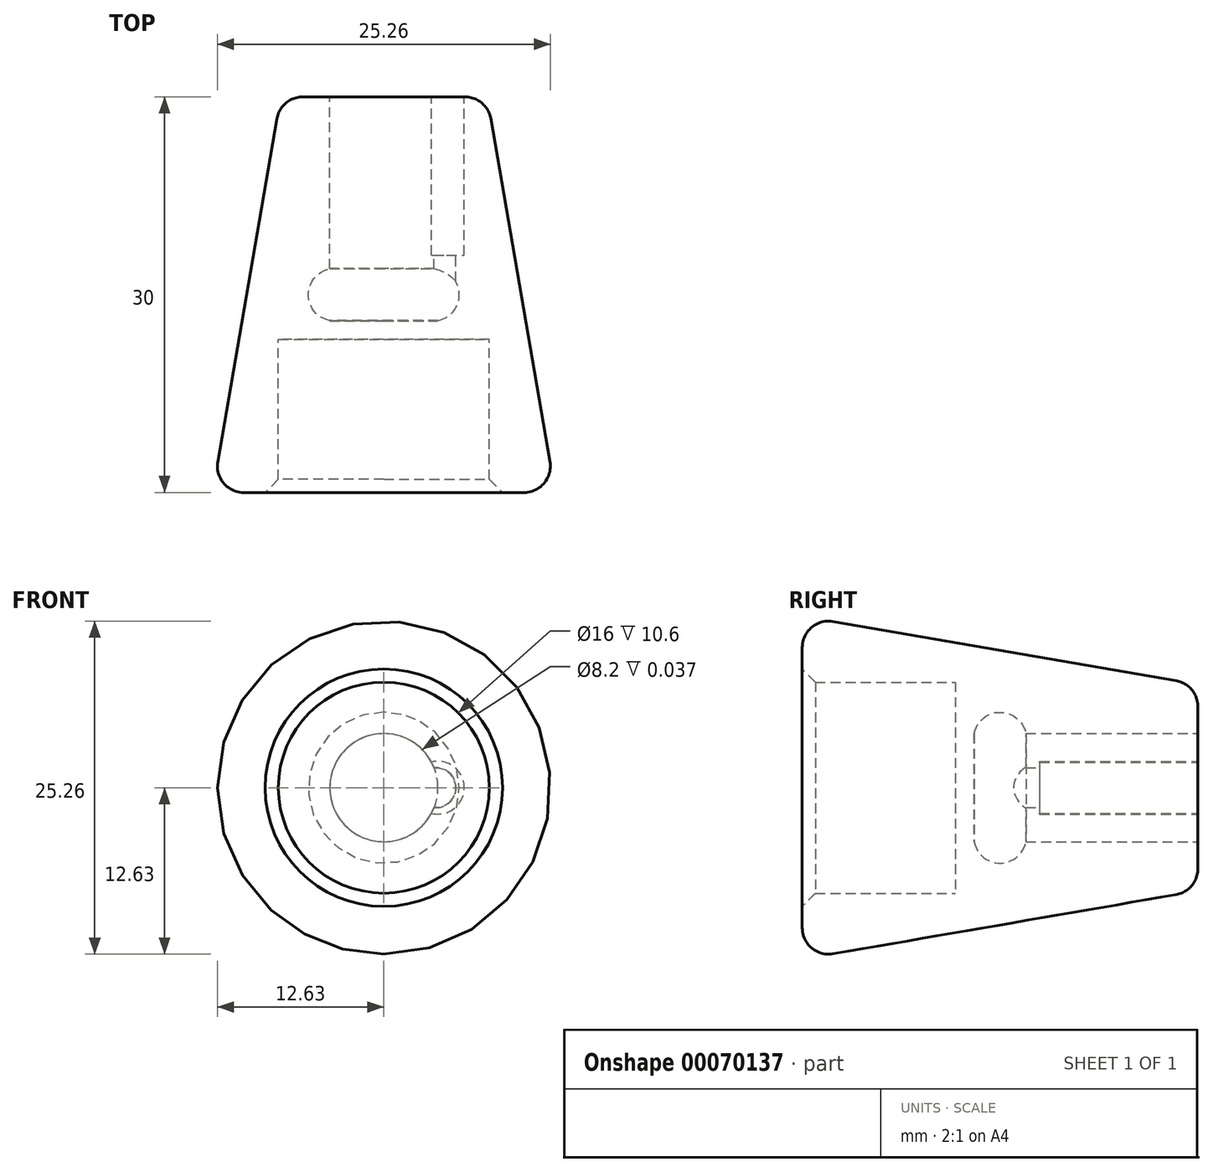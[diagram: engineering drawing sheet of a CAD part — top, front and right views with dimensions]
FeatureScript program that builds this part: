
annotation { "Feature Type Name" : "Feature", "Feature Type Description" : "" }
export const myFeature = defineFeature(function(context is Context, id is Id, definition is map)
    precondition{}
    {
        {
            var Q0;
            Q0=qCreatedBy(makeId("Top.planeOp"),FACE);
            var sketch = newSketch(context, id + "F0", { "sketchPlane" : qUnion([Q0])});
            skLineSegment(sketch, "E0.top", {"start": v(7.82, 15) * mm, "end": v(0, 15) * mm});
            skPoint(sketch, "E0.middle", {"position": v(0, 0) * mm});
            skLineSegment(sketch, "E1.bottom", {"start": v(8, -15) * mm, "end": v(7.82, -15) * mm});
            skLineSegment(sketch, "E1.top", {"start": v(8, -3.4) * mm, "end": v(0, -3.4) * mm});
            skLineSegment(sketch, "E1.left", {"start": v(8, -15) * mm, "end": v(8, -3.4) * mm});
            skLineSegment(sketch, "E1.right", {"start": v(-8, -15) * mm, "end": v(-8, -3.4) * mm});
            skPoint(sketch, "E1.middle", {"position": v(0, -9.2) * mm});
            skLineSegment(sketch, "E2", {"start": v(13, -15) * mm, "end": v(7.82, -15) * mm});
            skLineSegment(sketch, "E3", {"start": v(7.82, 15) * mm, "end": v(13, -15) * mm});
            skPoint(sketch, "E4.orphan", {"position": v(7.82, 0) * mm});
            skLineSegment(sketch, "E5", {"start": v(0, 15) * mm, "end": v(0, -3.4) * mm});
            skPoint(sketch, "E6.start.orphan", {"position": v(-7.82, 0) * mm});
            skLineSegment(sketch, "E7.trimOffspring", {"start": v(-7.82, -15) * mm, "end": v(-8, -15) * mm});
            skPoint(sketch, "E8.orphan", {"position": v(-7.82, 15) * mm});
            skPoint(sketch, "E9.trimOffspring.end.orphan", {"position": v(0, -15) * mm});
            skSolve(sketch);
        }
        {
            var Q0;
            Q0=makeQuery(id+"F0.imprint","IMPRINT",FACE,{"disambiguationData":[TD([[makeQuery(id+"F0.imprint","IMPRINT",EDGE,{"derivedFrom":sQuery(id+"F0.wireOp",EDGE,"E0.top")}),1.0]])]});
            var Q1;
            Q1=sQuery(id+"F0.wireOp",EDGE,"E5");
            revolve(context, id + "F1", {"entities" : qUnion([Q0]), "axis" : qUnion([Q1]), "revolveType" : RevolveType.FULL});
        }
        {
            var Q0;
            Q0=makeQuery(id+"F1.opRevolve","SWEPT_FACE",FACE,{"disambiguationData":[OSD([sQuery(id+"F0.wireOp",EDGE,"E0.top")])]});
            var sketch = newSketch(context, id + "F2", { "sketchPlane" : qUnion([Q0])});
            skCircle(sketch, "E10", {"center": v(0, 0) * mm, "radius": 4.1 * mm});
            skSolve(sketch);
        }
        {
            var Q0;
            Q0 = qSketchRegion(id + "F2", true);
            extrude(context, id + "F3", {"entities" : qUnion([Q0]), "operationType" : NewBodyOperationType.REMOVE, "oppositeDirection" : true, "depth" : 17 * mm});
        }
        {
            var Q0;
            Q0=qCreatedBy(makeId("Right.planeOp"),FACE);
            var sketch = newSketch(context, id + "F4", { "sketchPlane" : qUnion([Q0])});
            skCircle(sketch, "E11", {"center": v(0, 3.72) * mm, "radius": 2 * mm});
            skSolve(sketch);
        }
        {
            var Q0;
            Q0 = qSketchRegion(id + "F4", true);
            var Q1;
            Q1=makeQuery(id+"F3.boolean.opBoolean","COPY",EDGE,{"derivedFrom":makeQuery(id+"F3.opExtrude","CAP_EDGE",EDGE,{"disambiguationData":[OSD([sQuery(id+"F2.wireOp",EDGE,"E10")])],"isStart":false})});
            sweep(context, id + "F5", {"operationType" : NewBodyOperationType.REMOVE, "profiles" : qUnion([Q0]), "path" : qUnion([Q1])});
        }
        {
            var Q0;
            Q0=makeQuery(id+"F1.opRevolve","SWEPT_FACE",FACE,{"disambiguationData":[OSD([sQuery(id+"F0.wireOp",EDGE,"E0.top")])]});
            var sketch = newSketch(context, id + "F6", { "sketchPlane" : qUnion([Q0])});
            skCircle(sketch, "E12", {"center": v(-4.1, 0) * mm, "radius": 2 * mm});
            skSolve(sketch);
        }
        {
            var Q0;
            Q0 = qSketchRegion(id + "F6", true);
            extrude(context, id + "F7", {"entities" : qUnion([Q0]), "operationType" : NewBodyOperationType.REMOVE, "oppositeDirection" : true, "depth" : 12 * mm});
        }
        {
            var Q0;
            Q0=makeQuery(id+"F1.opRevolve","SWEPT_EDGE",EDGE,{"disambiguationData":[OSD([sQuery(id+"F0.wireOp",EDGE,"E0.top"),sQuery(id+"F0.wireOp",EDGE,"E3")])]});
            var Q1;
            Q1=makeQuery(id+"F1.opRevolve","SWEPT_EDGE",EDGE,{"disambiguationData":[OSD([sQuery(id+"F0.wireOp",EDGE,"E2"),sQuery(id+"F0.wireOp",EDGE,"E3")])]});
            fillet(context, id + "F8", {"entities" : qUnion([Q0, Q1]), "radius" : 2 * mm, "tangentPropagation" : true, "allowEdgeOverflow" : false});
        }
        {
            var Q0;
            Q0=makeQuery(id+"F1.opRevolve","SWEPT_EDGE",EDGE,{"disambiguationData":[OSD([sQuery(id+"F0.wireOp",EDGE,"E1.left"),sQuery(id+"F0.wireOp",EDGE,"E2")])]});
            chamfer(context, id + "F9", {"entities" : qUnion([Q0]), "width" : 1 * mm, "tangentPropagation" : true});
        }
        {
            var Q0;
            {var subQ0=sQuery(id+"F6.wireOp",EDGE,"E12");var subQ1=makeQuery(id+"F3.boolean.opBoolean","COPY",EDGE,{"derivedFrom":makeQuery(id+"F3.opExtrude","CAP_EDGE",EDGE,{"disambiguationData":[OSD([sQuery(id+"F2.wireOp",EDGE,"E10")])],"isStart":true})});var subQ2=makeQuery(id+"F6.imprint","INTERSECT",VERTEX,{"disambiguationData":[OD(0.0)],"derivedFrom":[subQ1,subQ0]});Q0=makeQuery(id+"F6.imprint","IMPRINT",FACE,{"disambiguationData":[TD([[makeQuery(id+"F6.imprint","IMPRINT",EDGE,{"disambiguationData":[TD([[subQ2,1.0]])],"derivedFrom":subQ0}),1.0]])]});}
            var sketch = newSketch(context, id + "F10", { "sketchPlane" : qUnion([Q0])});
            skCircle(sketch, "E13", {"center": v(-3.93, 0) * mm, "radius": 1.52 * mm});
            skSolve(sketch);
        }
        {
            var Q0;
            Q0 = qSketchRegion(id + "F10", true);
            extrude(context, id + "F11", {"entities" : qUnion([Q0]), "operationType" : NewBodyOperationType.REMOVE, "oppositeDirection" : true, "depth" : 14 * mm});
        }
    });
